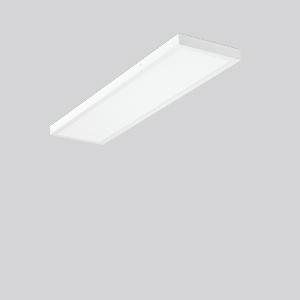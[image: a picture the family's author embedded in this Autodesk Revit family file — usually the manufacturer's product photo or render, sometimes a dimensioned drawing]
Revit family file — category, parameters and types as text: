
# Revit family: sidelite_eco_312378_002_1_76_c29c
name_source: partatom
category: Lighting Fixtures
units: mm (PartAtom-declared; Revit-internal decimal feet)

## family parameters
Cut with Voids When Loaded = No
Host = Face
Light Source = No
Part Type = Normal
Room Calculation Point = No
Round Connector Dimension = Use Diameter
Shared = No

## types (1)
- MultiLumen 1 (1 x LED Modul 840, 3500 lm, 4000)
    Apparent Load = 29 VA
    CIE Flux Codes = 47 79 96 100 100
    Color Rendering = 80
    Color Temperature = 4000
    Default Elevation = 1800 mm
    Description = Series: SIDELITE ECO
Highly economical surface mounted luminaire with progressive LED technology. Luminaire frame: aluminium, powder-coated. Mounting frame: sheet steel, powder-coated. Diffuser: plastic, opal. Lightguide and diffuser made of non-yellowing plastic (PMMA). Lateral light emission (RZB SIDELITE technology) for homogeneous light distribution. Driver integrated. MultiLumen: 4 steps adjustable luminous flux. Factory setting is the lowest offered step. Qualified for use in the food and drink industry. 
Colour: white
Length: 1202 mm
Width: 302 mm
Height: 47 mm
Lamp: LED
Socket: without socket
Colour temperature: 4000K
Colour rendering index (CRI): 80
System power: 29 W
Rated luminous flux: 3500 lm
Luminous efficiency: 121 lm/W
System power 2: 33 W
Rated luminous flux 2: 3850 lm
Luminous efficiency 2: 117 lm/W
System power 3: 35 W
Rated luminous flux 3: 4050 lm
Luminous efficiency 3: 116 lm/W
System power 4: 38 W
Rated luminous flux 4: 4400 lm
Luminous efficiency 4: 116 lm/W
Control gear: Converter, dimmable, DALI
Protection class: II
Type of protection: IP 40
    Height = 47 mm
    Lamp = 1 x LED Modul 840
    Lamp Light Flux = 3500 lm
    Lamp count = 1
    Length = 1202 mm
    Lifetime = 50000 h
    Luminous efficacy = 121 lm/W
    Manufacturer = RZB
    ModVariant = No
    Model = 312378.002.1.76
    Mounting Place = Ceiling
    Mounting Type = Surface mounted
    Number of Poles = 1
    OnlyDefault = Yes
    Power Factor = 1
    Product Name = SIDELITE ECO
    Product group = Surface mounted modular luminaires
    ProductGroupID = 306
    Protection Class = Protection class II
    Protection Degree = IP 40
    RLX_Detail_Level = 1
    RLX_Emergency_Light_Flux = 0 lm
    RLX_Emergency_Type = 0
    RLX_Emergency_Type_DB = No
    RlxData = <blob elided: 20717 chars, md5=d2d201ef>
    Socket = socket
    Standby Power = 0 W
    System Light Flux = 3500 lm
    System Power = 29 W
    Type Comments = MultiLumen 1
    Type Image = 312378.002.jpg
    URL = http://relux.com
    VarID = multilumen_1
    Voltage = 230 V
    Voltage Range = 220-240 V
    Weight = 0.00 kg
    Width = 302 mm

## geometry (parser evidence)
native form markers: Blend x4, Sweep x11
no freeform markers — native parametric forms only
